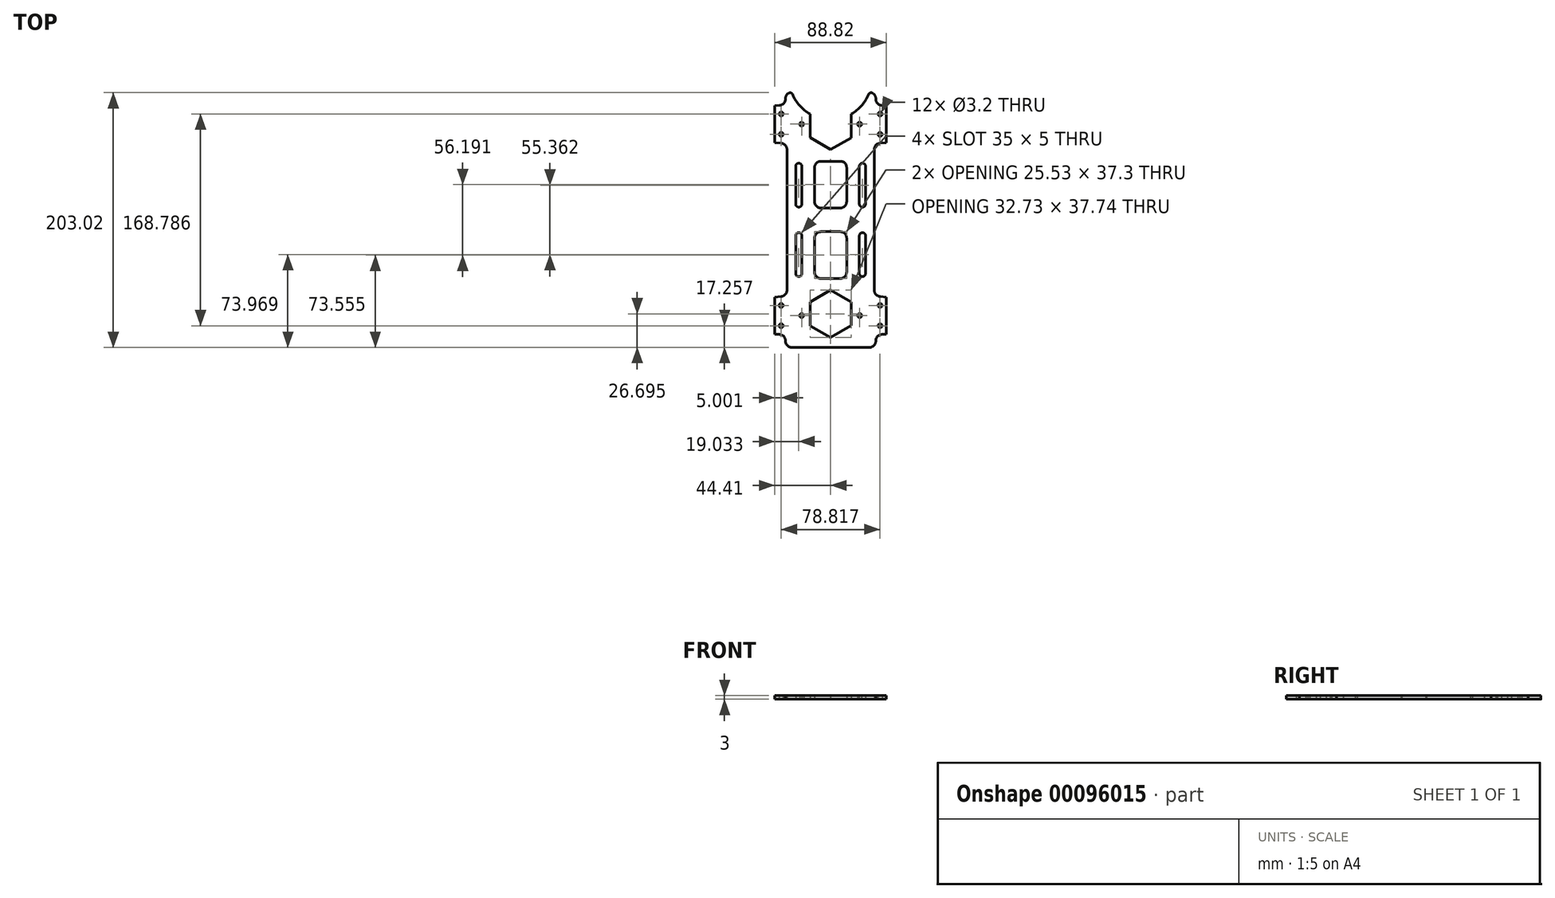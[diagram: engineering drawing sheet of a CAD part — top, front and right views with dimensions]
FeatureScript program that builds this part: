
annotation { "Feature Type Name" : "Feature", "Feature Type Description" : "" }
export const myFeature = defineFeature(function(context is Context, id is Id, definition is map)
    precondition{}
    {
        {
            var Q0;
            Q0=qCreatedBy(makeId("Top.planeOp"),FACE);
            var sketch = newSketch(context, id + "F0", { "sketchPlane" : qUnion([Q0])});
            skCircle(sketch, "E0", {"center": v(-39.4, -84.4) * mm, "radius": 1.6 * mm});
            skCircle(sketch, "E1", {"center": v(-39.4, -68.2) * mm, "radius": 1.6 * mm});
            skCircle(sketch, "E2", {"center": v(-23.11, -76.3) * mm, "radius": 1.6 * mm});
            skLineSegment(sketch, "E3", {"start": v(-39.4, -84.4) * mm, "end": v(-23.11, -76.3) * mm, "construction": true});
            skLineSegment(sketch, "E4", {"start": v(-23.11, -76.3) * mm, "end": v(-39.4, -68.2) * mm, "construction": true});
            skLineSegment(sketch, "E5", {"start": v(-39.4, -84.4) * mm, "end": v(-39.4, -68.2) * mm, "construction": true});
            skLineSegment(sketch, "E6", {"start": v(-44.4, -91.06) * mm, "end": v(-44.4, -61.53) * mm});
            skLineSegment(sketch, "E7", {"start": v(-44.4, -61.53) * mm, "end": v(-39.45, -61.18) * mm});
            skLineSegment(sketch, "E8", {"start": v(-34.8, -56.2) * mm, "end": v(-34.8, 0) * mm});
            skLineSegment(sketch, "E9.MirrorCS", {"start": v(-44.4, -91.06) * mm, "end": v(-40.65, -91.32) * mm});
            skPoint(sketch, "E10.visualSharp", {"position": v(-34.8, -60.85) * mm});
            skArc(sketch, "E10.filletArc", {"start": v(-39.45, -61.18) * mm, "mid": v(-36.14, -59.6) * mm, "end": v(-34.8, -56.2) * mm});
            skLineSegment(sketch, "E11", {"start": v(-36, -96.31) * mm, "end": v(-36, -96.65) * mm});
            skLineSegment(sketch, "E12", {"start": v(-31, -101.65) * mm, "end": v(0, -101.65) * mm});
            skPoint(sketch, "E13.visualSharp", {"position": v(-36, -101.65) * mm});
            skArc(sketch, "E13.filletArc", {"start": v(-36, -96.65) * mm, "mid": v(-34.54, -100.18) * mm, "end": v(-31, -101.65) * mm});
            skPoint(sketch, "E14.visualSharp", {"position": v(-36, -91.65) * mm});
            skArc(sketch, "E14.filletArc", {"start": v(-36, -96.31) * mm, "mid": v(-37.34, -92.9) * mm, "end": v(-40.65, -91.32) * mm});
            skCircle(sketch, "E15.MirrorC", {"center": v(23.11, -76.3) * mm, "radius": 1.6 * mm});
            skCircle(sketch, "E16.MirrorC", {"center": v(39.4, -68.2) * mm, "radius": 1.6 * mm});
            skCircle(sketch, "E17.MirrorC", {"center": v(39.4, -84.4) * mm, "radius": 1.6 * mm});
            skArc(sketch, "E18.MirrorCS", {"start": v(39.45, -61.18) * mm, "mid": v(36.14, -59.6) * mm, "end": v(34.8, -56.2) * mm});
            skLineSegment(sketch, "E19.MirrorCS", {"start": v(44.4, -91.06) * mm, "end": v(40.65, -91.32) * mm});
            skLineSegment(sketch, "E20.MirrorCS", {"start": v(36, -96.31) * mm, "end": v(36, -96.65) * mm});
            skArc(sketch, "E21.MirrorCS", {"start": v(36, -96.31) * mm, "mid": v(37.34, -92.9) * mm, "end": v(40.65, -91.32) * mm});
            skArc(sketch, "E22.MirrorCS", {"start": v(36, -96.65) * mm, "mid": v(34.54, -100.18) * mm, "end": v(31, -101.65) * mm});
            skLineSegment(sketch, "E23.MirrorCS", {"start": v(44.4, -61.53) * mm, "end": v(39.45, -61.18) * mm});
            skLineSegment(sketch, "E24.MirrorCS", {"start": v(39.4, -84.4) * mm, "end": v(39.4, -68.2) * mm, "construction": true});
            skLineSegment(sketch, "E25.MirrorCS", {"start": v(39.4, -84.4) * mm, "end": v(23.11, -76.3) * mm, "construction": true});
            skPoint(sketch, "E26.MirrorP", {"position": v(36, -101.65) * mm});
            skLineSegment(sketch, "E27.MirrorCS", {"start": v(23.11, -76.3) * mm, "end": v(39.4, -68.2) * mm, "construction": true});
            skLineSegment(sketch, "E28.MirrorCS", {"start": v(31, -101.65) * mm, "end": v(0, -101.65) * mm});
            skLineSegment(sketch, "E29.MirrorCS", {"start": v(34.8, -56.2) * mm, "end": v(34.8, 0) * mm});
            skPoint(sketch, "E30.MirrorP", {"position": v(36, -91.65) * mm});
            skPoint(sketch, "E31.MirrorP", {"position": v(34.8, -60.85) * mm});
            skCircle(sketch, "E32.MirrorC", {"center": v(-23.11, 76.3) * mm, "radius": 1.6 * mm});
            skCircle(sketch, "E33.MirrorC", {"center": v(-39.4, 84.4) * mm, "radius": 1.6 * mm});
            skCircle(sketch, "E34.MirrorC", {"center": v(-39.4, 68.2) * mm, "radius": 1.6 * mm});
            skArc(sketch, "E35.MirrorCS", {"start": v(-36, 96.31) * mm, "mid": v(-37.34, 92.9) * mm, "end": v(-40.65, 91.32) * mm});
            skLineSegment(sketch, "E36.MirrorCS", {"start": v(-44.4, 61.53) * mm, "end": v(-39.45, 61.18) * mm});
            skArc(sketch, "E37.MirrorCS", {"start": v(36, 96.65) * mm, "mid": v(34.54, 100.18) * mm, "end": v(31, 101.65) * mm});
            skCircle(sketch, "E38.MirrorC", {"center": v(39.4, 68.2) * mm, "radius": 1.6 * mm});
            skLineSegment(sketch, "E39.MirrorCS", {"start": v(36, 96.31) * mm, "end": v(36, 96.65) * mm});
            skArc(sketch, "E40.MirrorCS", {"start": v(-36, 96.65) * mm, "mid": v(-34.54, 100.18) * mm, "end": v(-31, 101.65) * mm});
            skArc(sketch, "E41.MirrorCS", {"start": v(36, 96.31) * mm, "mid": v(37.34, 92.9) * mm, "end": v(40.65, 91.32) * mm});
            skArc(sketch, "E42.MirrorCS", {"start": v(-39.45, 61.18) * mm, "mid": v(-36.14, 59.6) * mm, "end": v(-34.8, 56.2) * mm});
            skLineSegment(sketch, "E43.MirrorCS", {"start": v(-44.4, 91.06) * mm, "end": v(-40.65, 91.32) * mm});
            skCircle(sketch, "E44.MirrorC", {"center": v(23.11, 76.3) * mm, "radius": 1.6 * mm});
            skLineSegment(sketch, "E45.MirrorCS", {"start": v(-36, 96.31) * mm, "end": v(-36, 96.65) * mm});
            skCircle(sketch, "E46.MirrorC", {"center": v(39.4, 84.4) * mm, "radius": 1.6 * mm});
            skLineSegment(sketch, "E47.MirrorCS", {"start": v(44.4, 91.06) * mm, "end": v(40.65, 91.32) * mm});
            skArc(sketch, "E48.MirrorCS", {"start": v(39.45, 61.18) * mm, "mid": v(36.14, 59.6) * mm, "end": v(34.8, 56.2) * mm});
            skLineSegment(sketch, "E49.MirrorCS", {"start": v(44.4, 61.53) * mm, "end": v(39.45, 61.18) * mm});
            skLineSegment(sketch, "E50.MirrorCS", {"start": v(-39.4, 84.4) * mm, "end": v(-39.4, 68.2) * mm, "construction": true});
            skPoint(sketch, "E51.MirrorP", {"position": v(-34.8, 60.85) * mm});
            skLineSegment(sketch, "E52.MirrorCS", {"start": v(-39.4, 84.4) * mm, "end": v(-23.11, 76.3) * mm, "construction": true});
            skLineSegment(sketch, "E53.MirrorCS", {"start": v(-23.11, 76.3) * mm, "end": v(-39.4, 68.2) * mm, "construction": true});
            skPoint(sketch, "E54.MirrorP", {"position": v(34.8, 60.85) * mm});
            skLineSegment(sketch, "E55.MirrorCS", {"start": v(39.4, 84.4) * mm, "end": v(39.4, 68.2) * mm, "construction": true});
            skPoint(sketch, "E56.MirrorP", {"position": v(-36, 91.65) * mm});
            skLineSegment(sketch, "E57.MirrorCS", {"start": v(-34.8, 56.2) * mm, "end": v(-34.8, 0) * mm});
            skPoint(sketch, "E58.MirrorP", {"position": v(36, 101.65) * mm});
            skLineSegment(sketch, "E59.MirrorCS", {"start": v(23.11, 76.3) * mm, "end": v(39.4, 68.2) * mm, "construction": true});
            skPoint(sketch, "E60.MirrorP", {"position": v(-36, 101.65) * mm});
            skLineSegment(sketch, "E61.MirrorCS", {"start": v(34.8, 56.2) * mm, "end": v(34.8, 0) * mm});
            skLineSegment(sketch, "E62.MirrorCS", {"start": v(39.4, 84.4) * mm, "end": v(23.11, 76.3) * mm, "construction": true});
            skPoint(sketch, "E63.MirrorP", {"position": v(36, 91.65) * mm});
            skLineSegment(sketch, "E64", {"start": v(-34.8, 0) * mm, "end": v(0, 0) * mm, "construction": true});
            skLineSegment(sketch, "E65.bottom", {"start": v(25.38, -45.18) * mm, "end": v(25.38, -45.18) * mm});
            skLineSegment(sketch, "E65.top", {"start": v(25.38, -10.18) * mm, "end": v(25.38, -10.18) * mm});
            skLineSegment(sketch, "E65.left", {"start": v(22.88, -42.68) * mm, "end": v(22.88, -12.68) * mm});
            skLineSegment(sketch, "E65.right", {"start": v(27.88, -42.68) * mm, "end": v(27.88, -12.68) * mm});
            skPoint(sketch, "E65.middle.positionSnap0", {"position": v(34.8, -28.1) * mm});
            skPoint(sketch, "E65.centerSnap0", {"position": v(34.8, -28.1) * mm});
            skPoint(sketch, "E66.visualSharp", {"position": v(22.88, -10.18) * mm});
            skArc(sketch, "E66.filletArc", {"start": v(25.38, -10.18) * mm, "mid": v(23.6, -10.91) * mm, "end": v(22.88, -12.68) * mm});
            skPoint(sketch, "E67.visualSharp", {"position": v(27.88, -10.18) * mm});
            skArc(sketch, "E67.filletArc", {"start": v(27.88, -12.68) * mm, "mid": v(27.15, -10.91) * mm, "end": v(25.38, -10.18) * mm});
            skPoint(sketch, "E68.visualSharp", {"position": v(27.88, -45.18) * mm});
            skArc(sketch, "E68.filletArc", {"start": v(25.38, -45.18) * mm, "mid": v(27.15, -44.45) * mm, "end": v(27.88, -42.68) * mm});
            skPoint(sketch, "E69.visualSharp", {"position": v(22.88, -45.18) * mm});
            skArc(sketch, "E69.filletArc", {"start": v(22.88, -42.68) * mm, "mid": v(23.6, -44.45) * mm, "end": v(25.38, -45.18) * mm});
            skLineSegment(sketch, "E70", {"start": v(34.8, 0) * mm, "end": v(0, 0) * mm, "construction": true});
            skLineSegment(sketch, "E71", {"start": v(17.4, 0) * mm, "end": v(17.4, -61.5) * mm, "construction": true});
            skLineSegment(sketch, "E72", {"start": v(0, 0) * mm, "end": v(0, -74.96) * mm, "construction": true});
            skLineSegment(sketch, "E73.MirrorCS", {"start": v(-25.38, -10.18) * mm, "end": v(-25.38, -10.18) * mm});
            skLineSegment(sketch, "E74.MirrorCS", {"start": v(-25.38, -45.18) * mm, "end": v(-25.38, -45.18) * mm});
            skArc(sketch, "E75.MirrorCS", {"start": v(-25.38, -45.18) * mm, "mid": v(-27.15, -44.45) * mm, "end": v(-27.88, -42.68) * mm});
            skArc(sketch, "E76.MirrorCS", {"start": v(-22.88, -42.68) * mm, "mid": v(-23.6, -44.45) * mm, "end": v(-25.38, -45.18) * mm});
            skArc(sketch, "E77.MirrorCS", {"start": v(-27.88, -12.68) * mm, "mid": v(-27.15, -10.91) * mm, "end": v(-25.38, -10.18) * mm});
            skArc(sketch, "E78.MirrorCS", {"start": v(-25.38, -10.18) * mm, "mid": v(-23.6, -10.91) * mm, "end": v(-22.88, -12.68) * mm});
            skPoint(sketch, "E79.MirrorP", {"position": v(-22.88, -10.18) * mm});
            skPoint(sketch, "E80.MirrorP", {"position": v(-22.88, -45.18) * mm});
            skPoint(sketch, "E81.MirrorP", {"position": v(-27.88, -10.18) * mm});
            skLineSegment(sketch, "E82.MirrorCS", {"start": v(-22.88, -42.68) * mm, "end": v(-22.88, -12.68) * mm});
            skLineSegment(sketch, "E83.MirrorCS", {"start": v(-27.88, -42.68) * mm, "end": v(-27.88, -12.68) * mm});
            skPoint(sketch, "E84.MirrorP", {"position": v(-27.88, -45.18) * mm});
            skLineSegment(sketch, "E85.MirrorCS", {"start": v(-25.38, 45.18) * mm, "end": v(-25.38, 45.18) * mm});
            skLineSegment(sketch, "E86.MirrorCS", {"start": v(-25.38, 10.18) * mm, "end": v(-25.38, 10.18) * mm});
            skArc(sketch, "E87.MirrorCS", {"start": v(-25.38, 10.18) * mm, "mid": v(-23.6, 10.91) * mm, "end": v(-22.88, 12.68) * mm});
            skArc(sketch, "E88.MirrorCS", {"start": v(-27.88, 12.68) * mm, "mid": v(-27.15, 10.91) * mm, "end": v(-25.38, 10.18) * mm});
            skArc(sketch, "E89.MirrorCS", {"start": v(-25.38, 45.18) * mm, "mid": v(-27.15, 44.45) * mm, "end": v(-27.88, 42.68) * mm});
            skArc(sketch, "E90.MirrorCS", {"start": v(-22.88, 42.68) * mm, "mid": v(-23.6, 44.45) * mm, "end": v(-25.38, 45.18) * mm});
            skLineSegment(sketch, "E91.MirrorCS", {"start": v(25.38, 10.18) * mm, "end": v(25.38, 10.18) * mm});
            skLineSegment(sketch, "E92.MirrorCS", {"start": v(25.38, 45.18) * mm, "end": v(25.38, 45.18) * mm});
            skArc(sketch, "E93.MirrorCS", {"start": v(25.38, 45.18) * mm, "mid": v(27.15, 44.45) * mm, "end": v(27.88, 42.68) * mm});
            skArc(sketch, "E94.MirrorCS", {"start": v(27.88, 12.68) * mm, "mid": v(27.15, 10.91) * mm, "end": v(25.38, 10.18) * mm});
            skArc(sketch, "E95.MirrorCS", {"start": v(25.38, 10.18) * mm, "mid": v(23.6, 10.91) * mm, "end": v(22.88, 12.68) * mm});
            skArc(sketch, "E96.MirrorCS", {"start": v(22.88, 42.68) * mm, "mid": v(23.6, 44.45) * mm, "end": v(25.38, 45.18) * mm});
            skPoint(sketch, "E97.MirrorP", {"position": v(34.8, 28.1) * mm});
            skLineSegment(sketch, "E98.MirrorCS", {"start": v(22.88, 42.68) * mm, "end": v(22.88, 12.68) * mm});
            skPoint(sketch, "E99.MirrorP", {"position": v(27.88, 10.18) * mm});
            skPoint(sketch, "E100.MirrorP", {"position": v(22.88, 10.18) * mm});
            skPoint(sketch, "E101.MirrorP", {"position": v(-22.88, 10.18) * mm});
            skPoint(sketch, "E102.MirrorP", {"position": v(22.88, 45.18) * mm});
            skLineSegment(sketch, "E103.MirrorCS", {"start": v(-27.88, 42.68) * mm, "end": v(-27.88, 12.68) * mm});
            skPoint(sketch, "E104.MirrorP", {"position": v(-27.88, 10.18) * mm});
            skLineSegment(sketch, "E105.MirrorCS", {"start": v(27.88, 42.68) * mm, "end": v(27.88, 12.68) * mm});
            skPoint(sketch, "E106.MirrorP", {"position": v(27.88, 45.18) * mm});
            skPoint(sketch, "E107.MirrorP", {"position": v(-22.88, 45.18) * mm});
            skPoint(sketch, "E108.MirrorP", {"position": v(-27.88, 45.18) * mm});
            skLineSegment(sketch, "E109.MirrorCS", {"start": v(-22.88, 42.68) * mm, "end": v(-22.88, 12.68) * mm});
            skCircle(sketch, "E110.cCircle", {"center": v(0, -74.96) * mm, "radius": 16.34 * mm, "construction": true});
            skLineSegment(sketch, "E110.0", {"start": v(16.36, -84.35) * mm, "end": v(0.05, -93.82) * mm});
            skLineSegment(sketch, "E110.1", {"start": v(0.05, -93.82) * mm, "end": v(-16.32, -84.43) * mm});
            skLineSegment(sketch, "E110.2", {"start": v(-16.32, -84.43) * mm, "end": v(-16.36, -65.56) * mm});
            skLineSegment(sketch, "E110.3", {"start": v(-16.36, -65.56) * mm, "end": v(-0.05, -56.09) * mm});
            skLineSegment(sketch, "E110.4", {"start": v(-0.05, -56.09) * mm, "end": v(16.32, -65.48) * mm});
            skLineSegment(sketch, "E110.5", {"start": v(16.32, -65.48) * mm, "end": v(16.36, -84.35) * mm});
            skPoint(sketch, "E110.0.midPoint", {"position": v(8.2, -89.09) * mm});
            skLineSegment(sketch, "E111.MirrorCS", {"start": v(44.4, -91.06) * mm, "end": v(44.4, -61.53) * mm});
            skLineSegment(sketch, "E112.MirrorCS", {"start": v(-44.4, 91.06) * mm, "end": v(-44.4, 61.53) * mm});
            skLineSegment(sketch, "E113.MirrorCS", {"start": v(44.4, 91.06) * mm, "end": v(44.4, 61.53) * mm});
            skLineSegment(sketch, "E114.bottom", {"start": v(7.76, -46.74) * mm, "end": v(-7.76, -46.74) * mm});
            skLineSegment(sketch, "E114.top", {"start": v(7.76, -9.45) * mm, "end": v(-7.76, -9.45) * mm});
            skLineSegment(sketch, "E114.left", {"start": v(12.76, -41.74) * mm, "end": v(12.76, -14.45) * mm});
            skLineSegment(sketch, "E114.right", {"start": v(-12.76, -41.74) * mm, "end": v(-12.76, -14.45) * mm});
            skPoint(sketch, "E114.middle", {"position": v(0, -28.1) * mm});
            skPoint(sketch, "E114.middle.positionSnap0", {"position": v(-34.8, -28.1) * mm});
            skPoint(sketch, "E114.centerSnap0", {"position": v(-34.8, -28.1) * mm});
            skPoint(sketch, "E115.visualSharp", {"position": v(-12.76, -9.45) * mm});
            skArc(sketch, "E115.filletArc", {"start": v(-7.76, -9.45) * mm, "mid": v(-11.3, -10.91) * mm, "end": v(-12.76, -14.45) * mm});
            skPoint(sketch, "E116.visualSharp", {"position": v(-12.76, -46.74) * mm});
            skArc(sketch, "E116.filletArc", {"start": v(-12.76, -41.74) * mm, "mid": v(-11.3, -45.28) * mm, "end": v(-7.76, -46.74) * mm});
            skPoint(sketch, "E117.visualSharp", {"position": v(12.76, -46.74) * mm});
            skArc(sketch, "E117.filletArc", {"start": v(7.76, -46.74) * mm, "mid": v(11.3, -45.28) * mm, "end": v(12.76, -41.74) * mm});
            skPoint(sketch, "E118.visualSharp", {"position": v(12.76, -9.45) * mm});
            skArc(sketch, "E118.filletArc", {"start": v(12.76, -14.45) * mm, "mid": v(11.3, -10.91) * mm, "end": v(7.76, -9.45) * mm});
            skLineSegment(sketch, "E119.MirrorCS", {"start": v(7.76, 9.45) * mm, "end": v(-7.76, 9.45) * mm});
            skArc(sketch, "E120.MirrorCS", {"start": v(-7.76, 9.45) * mm, "mid": v(-11.3, 10.91) * mm, "end": v(-12.76, 14.45) * mm});
            skLineSegment(sketch, "E121.MirrorCS", {"start": v(-12.76, 41.74) * mm, "end": v(-12.76, 14.45) * mm});
            skArc(sketch, "E122.MirrorCS", {"start": v(-12.76, 41.74) * mm, "mid": v(-11.3, 45.28) * mm, "end": v(-7.76, 46.74) * mm});
            skLineSegment(sketch, "E123.MirrorCS", {"start": v(7.76, 46.74) * mm, "end": v(-7.76, 46.74) * mm});
            skArc(sketch, "E124.MirrorCS", {"start": v(7.76, 46.74) * mm, "mid": v(11.3, 45.28) * mm, "end": v(12.76, 41.74) * mm});
            skLineSegment(sketch, "E125.MirrorCS", {"start": v(12.76, 41.74) * mm, "end": v(12.76, 14.45) * mm});
            skArc(sketch, "E126.MirrorCS", {"start": v(12.76, 14.45) * mm, "mid": v(11.3, 10.91) * mm, "end": v(7.76, 9.45) * mm});
            skLineSegment(sketch, "E127", {"start": v(-31, 101.65) * mm, "end": v(31, 101.65) * mm});
            skLineSegment(sketch, "E128.MirrorCS", {"start": v(-16.36, 65.56) * mm, "end": v(-0.05, 56.09) * mm});
            skLineSegment(sketch, "E129.MirrorCS", {"start": v(-0.05, 56.09) * mm, "end": v(16.32, 65.48) * mm});
            skLineSegment(sketch, "E130.MirrorCS", {"start": v(16.32, 65.48) * mm, "end": v(16.36, 84.35) * mm});
            skLineSegment(sketch, "E131.MirrorCS", {"start": v(16.36, 84.35) * mm, "end": v(0.05, 93.82) * mm});
            skLineSegment(sketch, "E132.MirrorCS", {"start": v(0.05, 93.82) * mm, "end": v(-16.32, 84.43) * mm});
            skLineSegment(sketch, "E133.MirrorCS", {"start": v(-16.32, 84.43) * mm, "end": v(-16.36, 65.56) * mm});
            skSolve(sketch);
        }
        {
            var Q0;
            Q0=qSketchRegion(id+"F0",true);
            extrude(context, id + "F1", {"entities" : qUnion([Q0]), "depth" : 3 * mm});
        }
        {
            var Q0;
            Q0=qCreatedBy(makeId("Top.planeOp"),FACE);
            var sketch = newSketch(context, id + "F2", { "sketchPlane" : qUnion([Q0])});
            skLineSegment(sketch, "E134.0", {"start": v(-31, 101.65) * mm, "end": v(31, 101.65) * mm});
            skLineSegment(sketch, "E135.0", {"start": v(0.05, 93.82) * mm, "end": v(-16.32, 84.43) * mm});
            skLineSegment(sketch, "E136.0", {"start": v(16.36, 84.35) * mm, "end": v(0.05, 93.82) * mm});
            skArc(sketch, "E137", {"start": v(-31, 101.65) * mm, "mid": v(0, 80.01) * mm, "end": v(31, 101.65) * mm});
            skSolve(sketch);
        }
        {
            var Q0;
            Q0 = qSketchRegion(id + "F2", true);
            extrude(context, id + "F3", {"entities" : qUnion([Q0]), "operationType" : NewBodyOperationType.REMOVE, "depth" : 25 * mm});
        }
        {
            var Q0;
            {var subQ0=sQuery(id+"F2.wireOp",EDGE,"E137");var subQ1=sQuery(id+"F2.wireOp",EDGE,"E134.0");Q0=makeQuery(id+"F3.boolean.opBoolean","MERGE",EDGE,{"derivedFrom":[makeQuery(id+"F1.opExtrude","SWEPT_EDGE",EDGE,{"disambiguationData":[OSD([sQuery(id+"F0.wireOp",EDGE,"E37.MirrorCS"),sQuery(id+"F0.wireOp",EDGE,"E127")])]}),makeQuery(id+"F3.opExtrude","SWEPT_EDGE",EDGE,{"disambiguationData":[OSD([subQ1,subQ0]),TDD([makeQuery(id+"F2.imprint","INTERSECT",VERTEX,{"disambiguationData":[OD(1.0)],"derivedFrom":[subQ1,subQ0]})])]})]});}
            var Q1;
            {var subQ0=sQuery(id+"F2.wireOp",EDGE,"E137");var subQ1=sQuery(id+"F2.wireOp",EDGE,"E134.0");Q1=makeQuery(id+"F3.boolean.opBoolean","MERGE",EDGE,{"derivedFrom":[makeQuery(id+"F1.opExtrude","SWEPT_EDGE",EDGE,{"disambiguationData":[OSD([sQuery(id+"F0.wireOp",EDGE,"E40.MirrorCS"),sQuery(id+"F0.wireOp",EDGE,"E127")])]}),makeQuery(id+"F3.opExtrude","SWEPT_EDGE",EDGE,{"disambiguationData":[OSD([subQ1,subQ0]),TDD([makeQuery(id+"F2.imprint","INTERSECT",VERTEX,{"disambiguationData":[OD(0.0)],"derivedFrom":[subQ1,subQ0]})])]})]});}
            fillet(context, id + "F4", {"entities" : qUnion([Q0, Q1]), "radius" : 2 * mm, "tangentPropagation" : true, "allowEdgeOverflow" : false});
        }
    });
